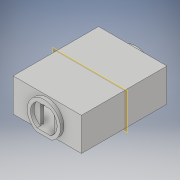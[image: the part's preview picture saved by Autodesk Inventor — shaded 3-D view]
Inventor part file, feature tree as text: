
AUTODESK INVENTOR PART (.ipt)
format: ipt  version: 2017 (Build 210142000, 142)  size: 281,600 bytes
history: native  units: in
note: dims shown in document units (in); Inventor stores cm internally (conversion verified against a paired STEP export)
features: extrude x9, sketch x7, mirror x3, other x1
ambient origin geometry x8: Origin, YZ Plane, XZ Plane, XY Plane, X Axis, Y Axis, Z Axis, Center Point
bodies: Solid1 (feature_tree), Solid2 (feature_tree)
feature tree (20):
  extrude  "floor"  Depth=25.0in
  extrude  "walls"  Depth=1.0in
  extrude  "doorframe"  Depth=1.0in
  extrude  "ceiling"  Depth=8.6667in TaperAngle=0.0deg
  extrude  "left door slot"  Depth=6.6667in
  mirror  "mirror door slot"
  mirror  "right door slot"
  sketch  "Sketch10"  dims[d20=8.6667in d21=0.0in d22=1.0in d23=0.0in]
  extrude  "corridor connect"  Depth=1.0in TaperAngle=0.0deg
  sketch  "Sketch11"  dims[d24=0.25in d25=0.5in d26=2.0in d27=0.0in d28=6.6667in d37=6.6667in d38=4.0in d39=1.0in d40=1.0in d41=0.0in d42=0.5833in d43=0.0625in d44=0.0625in d45=0.125in d46=0.25in d47=0.125in d48=45.0deg d49=0.0892in d50=0.0884in d51=1.0in d52=0.0in d53=1.0in d54=0.0in d55=1.0in d56=0.0in]
  extrude  "light"  Depth=0.5in
  extrude  "into wall light cut"  Depth=2.0in TaperAngle=0.0deg
  extrude  "into wall light join"  Depth=6.6667in
  other  "middle of the room"
  mirror  "Mirror2"
  sketch  "Sketch1"  dims[d0=20.0in d1=25.0in]
  sketch  "Sketch4"  dims[d2=1.0in d3=0.0in d11=1.0in]
  sketch  "Sketch5"  dims[d12=1.0in d13=1.0in]
  sketch  "Sketch7"  dims[d14=1.0in d15=8.6667in d16=0.0in]
  sketch  "Sketch8"  dims[d17=2.0in d18=6.6667in]
